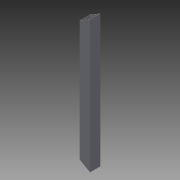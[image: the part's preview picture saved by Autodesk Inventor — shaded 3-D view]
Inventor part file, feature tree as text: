
AUTODESK INVENTOR PART (.ipt)
format: ipt  version: 2015 SP1 (Build 190203100, 203)  size: 90,112 bytes
history: native  units: in
note: dims shown in document units (in); Inventor stores cm internally (conversion verified against a paired STEP export)
features: extrude x2, sketch x2
ambient origin geometry x8: Origin, YZ Plane, XZ Plane, XY Plane, X Axis, Y Axis, Z Axis, Center Point
bodies: Solid1 (feature_tree)
feature tree (4):
  extrude  "Extrusion1"  Depth=2.0in
  extrude  "Extrusion2"  Depth=0.083in TaperAngle=0.0deg
  sketch  "Sketch1"  dims[d0=2.0in d1=2.0in]
  sketch  "Sketch2"  dims[d2=0.083in d3=28.0in d4=0.0in d5=30.0deg d6=30.0deg d7=24.0in d8=0.0in]
